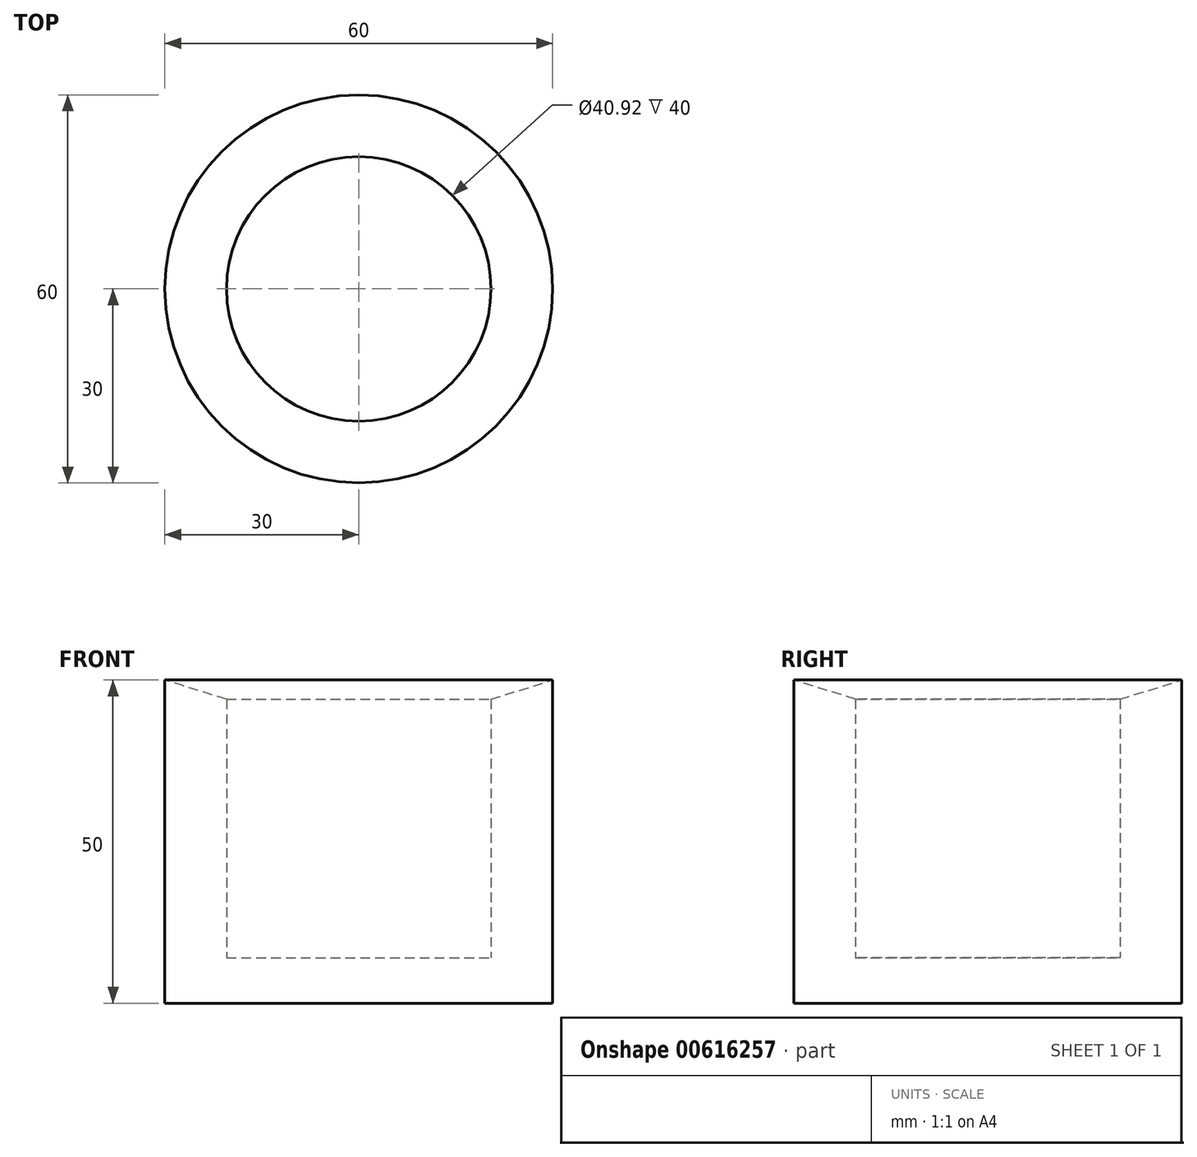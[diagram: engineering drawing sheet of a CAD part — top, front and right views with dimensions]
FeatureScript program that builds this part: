
annotation { "Feature Type Name" : "Feature", "Feature Type Description" : "" }
export const myFeature = defineFeature(function(context is Context, id is Id, definition is map)
    precondition{}
    {
        {
            var Q0;
            Q0=qCreatedBy(makeId("Front.planeOp"),FACE);
            var sketch = newSketch(context, id + "F0", { "sketchPlane" : qUnion([Q0])});
            skLineSegment(sketch, "E0", {"start": v(-30, 9.43) * mm, "end": v(-30, -40.57) * mm});
            skLineSegment(sketch, "E1", {"start": v(-30, -40.57) * mm, "end": v(0, -40.57) * mm});
            skLineSegment(sketch, "E2", {"start": v(0, -40.57) * mm, "end": v(0, -33.57) * mm});
            skLineSegment(sketch, "E3", {"start": v(0, -33.57) * mm, "end": v(-20.46, -33.57) * mm});
            skLineSegment(sketch, "E4", {"start": v(-20.46, -33.57) * mm, "end": v(-20.46, 6.43) * mm});
            skLineSegment(sketch, "E5", {"start": v(-20.46, 6.43) * mm, "end": v(-30, 9.43) * mm});
            skSolve(sketch);
        }
        {
            var Q0;
            Q0=makeQuery(id+"F0.imprint","IMPRINT",FACE,{"disambiguationData":[TD([[makeQuery(id+"F0.imprint","IMPRINT",EDGE,{"derivedFrom":sQuery(id+"F0.wireOp",EDGE,"E0")}),1.0]])]});
            var Q1;
            Q1=sQuery(id+"F0.wireOp",EDGE,"E2");
            revolve(context, id + "F1", {"entities" : qUnion([Q0]), "axis" : qUnion([Q1]), "revolveType" : RevolveType.FULL});
        }
    });
